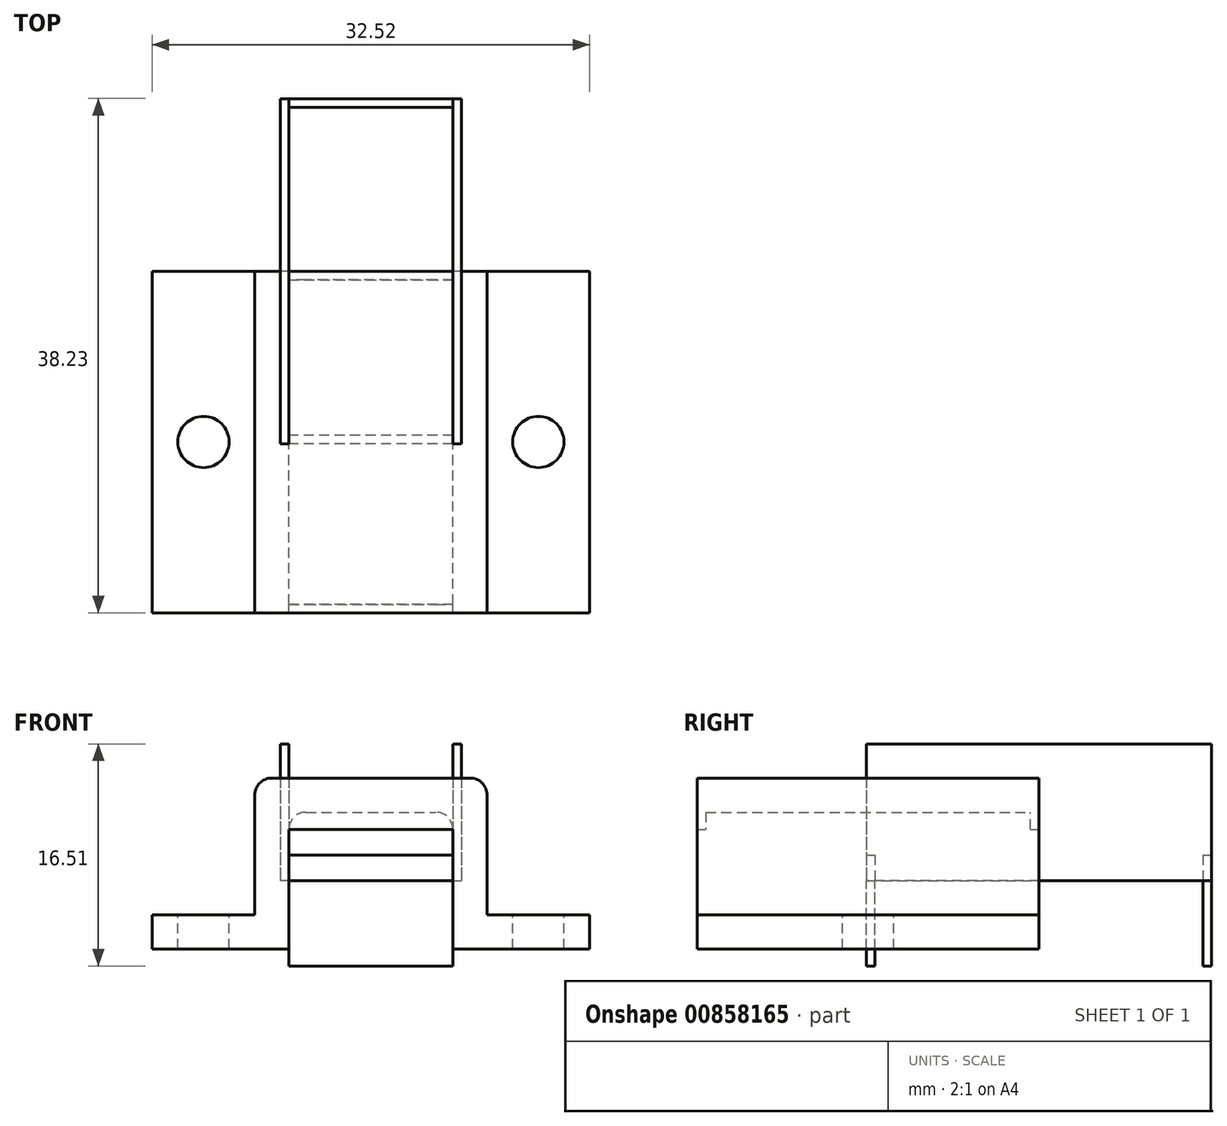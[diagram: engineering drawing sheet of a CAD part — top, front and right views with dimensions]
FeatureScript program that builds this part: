
annotation { "Feature Type Name" : "Feature", "Feature Type Description" : "" }
export const myFeature = defineFeature(function(context is Context, id is Id, definition is map)
    precondition{}
    {
        {
            var Q0;
            Q0=qCreatedBy(makeId("Top.planeOp"),FACE);
            var sketch = newSketch(context, id + "F0", { "sketchPlane" : qUnion([Q0])});
            skLineSegment(sketch, "E0.bottom", {"start": v(6.73, -12.2) * mm, "end": v(-6.73, -12.2) * mm});
            skLineSegment(sketch, "E0.top", {"start": v(6.73, 12.2) * mm, "end": v(-6.73, 12.2) * mm});
            skLineSegment(sketch, "E0.left", {"start": v(6.1, -12.83) * mm, "end": v(6.1, 12.83) * mm});
            skLineSegment(sketch, "E0.right", {"start": v(-6.1, -12.83) * mm, "end": v(-6.1, 12.83) * mm});
            skPoint(sketch, "E0.middle", {"position": v(0, 0) * mm});
            skPoint(sketch, "E1.orphan", {"position": v(-6.1, -12.2) * mm});
            skLineSegment(sketch, "E2", {"start": v(-6.1, -12.83) * mm, "end": v(-6.73, -12.83) * mm});
            skPoint(sketch, "E3.orphan", {"position": v(-6.1, 12.2) * mm});
            skPoint(sketch, "E4.orphan", {"position": v(6.1, 12.2) * mm});
            skLineSegment(sketch, "E5", {"start": v(-6.73, -12.83) * mm, "end": v(-6.73, 12.83) * mm});
            skLineSegment(sketch, "E6", {"start": v(-6.73, 12.83) * mm, "end": v(6.73, 12.83) * mm});
            skLineSegment(sketch, "E7", {"start": v(6.73, 12.83) * mm, "end": v(6.73, -12.2) * mm});
            skLineSegment(sketch, "E8", {"start": v(6.73, -12.83) * mm, "end": v(-6.1, -12.83) * mm});
            skLineSegment(sketch, "E9", {"start": v(6.73, -12.2) * mm, "end": v(6.73, -12.83) * mm});
            skPoint(sketch, "E10.orphan", {"position": v(6.1, -12.2) * mm});
            skSolve(sketch);
        }
        {
            var Q0;
            Q0=qCreatedBy(makeId("Front.planeOp"),FACE);
            var sketch = newSketch(context, id + "F1", { "sketchPlane" : qUnion([Q0])});
            skLineSegment(sketch, "E11.top", {"start": v(4.83, 5.08) * mm, "end": v(-4.83, 5.08) * mm});
            skLineSegment(sketch, "E11.left", {"start": v(6.1, -5.08) * mm, "end": v(6.1, 3.81) * mm});
            skLineSegment(sketch, "E11.right", {"start": v(-6.1, -5.08) * mm, "end": v(-6.1, 3.81) * mm});
            skPoint(sketch, "E11.middle", {"position": v(0, 0) * mm});
            skLineSegment(sketch, "E12", {"start": v(8.64, -2.54) * mm, "end": v(8.64, 6.35) * mm});
            skLineSegment(sketch, "E13", {"start": v(7.37, 7.62) * mm, "end": v(-7.37, 7.62) * mm});
            skLineSegment(sketch, "E14", {"start": v(-8.64, 6.35) * mm, "end": v(-8.64, -2.54) * mm});
            skLineSegment(sketch, "E15", {"start": v(-6.1, -5.08) * mm, "end": v(-16.26, -5.08) * mm});
            skLineSegment(sketch, "E16", {"start": v(-16.26, -5.08) * mm, "end": v(-16.26, -2.54) * mm});
            skLineSegment(sketch, "E17", {"start": v(-16.26, -2.54) * mm, "end": v(-8.64, -2.54) * mm});
            skLineSegment(sketch, "E18.MirrorCS", {"start": v(16.26, -2.54) * mm, "end": v(8.64, -2.54) * mm});
            skLineSegment(sketch, "E19.MirrorCS", {"start": v(6.1, -5.08) * mm, "end": v(16.26, -5.08) * mm});
            skLineSegment(sketch, "E20.MirrorCS", {"start": v(16.26, -5.08) * mm, "end": v(16.26, -2.54) * mm});
            skPoint(sketch, "E21.visualSharp", {"position": v(-6.1, 5.08) * mm});
            skArc(sketch, "E21.filletArc", {"start": v(-4.83, 5.08) * mm, "mid": v(-5.72, 4.7) * mm, "end": v(-6.1, 3.81) * mm});
            skPoint(sketch, "E22.visualSharp", {"position": v(6.1, 5.08) * mm});
            skArc(sketch, "E22.filletArc", {"start": v(6.1, 3.81) * mm, "mid": v(5.72, 4.7) * mm, "end": v(4.83, 5.08) * mm});
            skPoint(sketch, "E23.visualSharp", {"position": v(-8.64, 7.62) * mm});
            skArc(sketch, "E23.filletArc", {"start": v(-7.37, 7.62) * mm, "mid": v(-8.26, 7.25) * mm, "end": v(-8.64, 6.35) * mm});
            skPoint(sketch, "E24.visualSharp", {"position": v(8.64, 7.62) * mm});
            skArc(sketch, "E24.filletArc", {"start": v(8.64, 6.35) * mm, "mid": v(8.26, 7.25) * mm, "end": v(7.37, 7.62) * mm});
            skSolve(sketch);
        }
        {
            var Q0;
            Q0=makeQuery(id+"F1.imprint","IMPRINT",FACE,{"disambiguationData":[TD([[makeQuery(id+"F1.imprint","IMPRINT",EDGE,{"derivedFrom":sQuery(id+"F1.wireOp",EDGE,"E11.top")}),-1.0]])]});
            extrude(context, id + "F2", {"entities" : qUnion([Q0]), "depth" : 25.4 * mm, "offsetDistance" : 25.4 * mm});
        }
        {
            var Q0;
            Q0=makeQuery(id+"F2.opExtrude","SWEPT_FACE",FACE,{"disambiguationData":[OSD([sQuery(id+"F1.wireOp",EDGE,"E13")])]});
            var sketch = newSketch(context, id + "F3", { "sketchPlane" : qUnion([Q0])});
            skPoint(sketch, "E25", {"position": v(7.37, 0) * mm});
            skLineSegment(sketch, "E26.bottom", {"start": v(-7.38, 0) * mm, "end": v(7.37, 0) * mm});
            skLineSegment(sketch, "E26.top", {"start": v(-7.38, -0.63) * mm, "end": v(7.37, -0.63) * mm});
            skLineSegment(sketch, "E26.left", {"start": v(-7.38, 0) * mm, "end": v(-7.38, -0.63) * mm});
            skLineSegment(sketch, "E26.right", {"start": v(7.37, 0) * mm, "end": v(7.37, -0.63) * mm});
            skPoint(sketch, "E27", {"position": v(7.37, -25.4) * mm});
            skLineSegment(sketch, "E28.bottom", {"start": v(7.37, -25.4) * mm, "end": v(7.37, -25.4) * mm});
            skLineSegment(sketch, "E29.bottom", {"start": v(7.37, -25.4) * mm, "end": v(-7.37, -25.4) * mm});
            skLineSegment(sketch, "E29.top", {"start": v(7.37, -24.77) * mm, "end": v(-7.37, -24.77) * mm});
            skLineSegment(sketch, "E29.left", {"start": v(7.37, -25.4) * mm, "end": v(7.37, -24.77) * mm});
            skLineSegment(sketch, "E29.right", {"start": v(-7.37, -25.4) * mm, "end": v(-7.37, -24.77) * mm});
            skSolve(sketch);
        }
        {
            var Q0;
            {var subQ0=sQuery(id+"F3.wireOp",EDGE,"E26.right");Q0=makeQuery(id+"F3.imprint","IMPRINT",FACE,{"disambiguationData":[TD([[makeQuery(id+"F3.imprint","IMPRINT",EDGE,{"derivedFrom":subQ0}),1.0]])]});}
            var Q1;
            Q1=makeQuery(id+"F3.imprint","IMPRINT",FACE,{"disambiguationData":[TD([[makeQuery(id+"F3.imprint","IMPRINT",EDGE,{"derivedFrom":sQuery(id+"F3.wireOp",EDGE,"E28.bottom")}),-1.0]])]});
            extrude(context, id + "F4", {"entities" : qUnion([Q0, Q1]), "operationType" : NewBodyOperationType.ADD, "oppositeDirection" : true, "depth" : 3.8 * mm, "offsetDistance" : 25.4 * mm});
        }
        {
            var Q0;
            Q0=makeQuery(id+"F2.opExtrude","SWEPT_FACE",FACE,{"disambiguationData":[OSD([sQuery(id+"F1.wireOp",EDGE,"E17")])]});
            var sketch = newSketch(context, id + "F5", { "sketchPlane" : qUnion([Q0])});
            skLineSegment(sketch, "E30", {"start": v(-12.45, 0) * mm, "end": v(-12.45, -10.8) * mm});
            skPoint(sketch, "E31", {"position": v(-12.45, -12.7) * mm});
            skLineSegment(sketch, "E32.MirrorCS", {"start": v(12.45, 0) * mm, "end": v(12.45, -10.8) * mm});
            skPoint(sketch, "E33.MirrorP", {"position": v(12.45, -12.7) * mm});
            skCircle(sketch, "E34", {"center": v(-12.45, -12.7) * mm, "radius": 1.9 * mm});
            skCircle(sketch, "E35.MirrorC", {"center": v(12.45, -12.7) * mm, "radius": 1.9 * mm});
            skLineSegment(sketch, "E36.trimOffspring", {"start": v(-12.45, -14.6) * mm, "end": v(-12.45, -25.4) * mm});
            skLineSegment(sketch, "E37.trimOffspring", {"start": v(12.45, -14.6) * mm, "end": v(12.45, -25.4) * mm});
            skSolve(sketch);
        }
        {
            var Q0;
            Q0=makeQuery(id+"F3.imprint","IMPRINT",FACE,{"disambiguationData":[TD([[makeQuery(id+"F3.imprint","IMPRINT",EDGE,{"derivedFrom":sQuery(id+"F3.wireOp",EDGE,"E29.bottom")}),-1.0]])]});
            extrude(context, id + "F6", {"entities" : qUnion([Q0]), "operationType" : NewBodyOperationType.ADD, "oppositeDirection" : true, "depth" : 3.8 * mm, "offsetDistance" : 25.4 * mm});
        }
        {
            var Q0;
            Q0=sQuery(id+"F5.wireOp",VERTEX,"E31");
            var Q1;
            Q1=sQuery(id+"F5.wireOp",VERTEX,"E33.MirrorP");
            var Q2;
            Q2=makeQuery(id+"F2.opExtrude","SWEPT_BODY",BODY,{"disambiguationData":[OSD([sQuery(id+"F1.wireOp",EDGE,"E11.top"),sQuery(id+"F1.wireOp",EDGE,"E11.left"),sQuery(id+"F1.wireOp",EDGE,"E11.right"),sQuery(id+"F1.wireOp",EDGE,"E12"),sQuery(id+"F1.wireOp",EDGE,"E13"),sQuery(id+"F1.wireOp",EDGE,"E14"),sQuery(id+"F1.wireOp",EDGE,"E15"),sQuery(id+"F1.wireOp",EDGE,"E16"),sQuery(id+"F1.wireOp",EDGE,"E17"),sQuery(id+"F1.wireOp",EDGE,"E18.MirrorCS"),sQuery(id+"F1.wireOp",EDGE,"E19.MirrorCS"),sQuery(id+"F1.wireOp",EDGE,"E20.MirrorCS"),sQuery(id+"F1.wireOp",EDGE,"E21.filletArc"),sQuery(id+"F1.wireOp",EDGE,"E22.filletArc"),sQuery(id+"F1.wireOp",EDGE,"E23.filletArc"),sQuery(id+"F1.wireOp",EDGE,"E24.filletArc")])]});
            hole(context, id + "F7", {"style" : HoleStyle.SIMPLE, "endStyle" : HoleEndStyle.THROUGH, "holeDiameter" : 3.8 * mm, "majorDiameter" : 6.35 * mm, "isTappedThrough" : true, "tappedDepth" : 12.7 * mm, "tapClearance" : 3, "locations" : qUnion([Q0, Q1]), "scope" : qUnion([Q2])});
        }
        {
            var Q0;
            {var subQ5=sQuery(id+"F0.wireOp",EDGE,"E2");Q0=makeQuery(id+"F0.imprint","IMPRINT",FACE,{"disambiguationData":[TD([[makeQuery(id+"F0.imprint","IMPRINT",EDGE,{"derivedFrom":subQ5}),-1.0]])]});}
            var Q1;
            {var subQ0=sQuery(id+"F0.wireOp",EDGE,"E9");Q1=makeQuery(id+"F0.imprint","IMPRINT",FACE,{"disambiguationData":[TD([[makeQuery(id+"F0.imprint","IMPRINT",EDGE,{"derivedFrom":subQ0}),-1.0]])]});}
            var Q2;
            {var subQ0=sQuery(id+"F0.wireOp",EDGE,"E7");var subQ5=sQuery(id+"F0.wireOp",EDGE,"E0.top");var subQ6=makeQuery(id+"F0.imprint","INTERSECT",VERTEX,{"derivedFrom":[subQ5,subQ0]});Q2=makeQuery(id+"F0.imprint","IMPRINT",FACE,{"disambiguationData":[TD([[makeQuery(id+"F0.imprint","IMPRINT",EDGE,{"disambiguationData":[TD([[subQ6,-1.0]])],"derivedFrom":subQ5}),1.0]])]});}
            var Q3;
            {var subQ0=sQuery(id+"F0.wireOp",EDGE,"E7");var subQ1=sQuery(id+"F0.wireOp",EDGE,"E0.top");var subQ2=makeQuery(id+"F0.imprint","INTERSECT",VERTEX,{"derivedFrom":[subQ1,subQ0]});Q3=makeQuery(id+"F0.imprint","IMPRINT",FACE,{"disambiguationData":[TD([[makeQuery(id+"F0.imprint","IMPRINT",EDGE,{"disambiguationData":[TD([[subQ2,-1.0]])],"derivedFrom":subQ1}),-1.0]])]});}
            var Q4;
            {var subQ0=sQuery(id+"F0.wireOp",EDGE,"E5");var subQ1=sQuery(id+"F0.wireOp",EDGE,"E0.top");var subQ2=makeQuery(id+"F0.imprint","INTERSECT",VERTEX,{"derivedFrom":[subQ1,subQ0]});Q4=makeQuery(id+"F0.imprint","IMPRINT",FACE,{"disambiguationData":[TD([[makeQuery(id+"F0.imprint","IMPRINT",EDGE,{"disambiguationData":[TD([[subQ2,1.0]])],"derivedFrom":subQ1}),-1.0]])]});}
            var Q5;
            {var subQ0=sQuery(id+"F0.wireOp",EDGE,"E5");var subQ1=sQuery(id+"F0.wireOp",EDGE,"E0.bottom");var subQ2=makeQuery(id+"F0.imprint","INTERSECT",VERTEX,{"derivedFrom":[subQ1,subQ0]});Q5=makeQuery(id+"F0.imprint","IMPRINT",FACE,{"disambiguationData":[TD([[makeQuery(id+"F0.imprint","IMPRINT",EDGE,{"disambiguationData":[TD([[subQ2,1.0]])],"derivedFrom":subQ1}),-1.0]])]});}
            extrude(context, id + "F8", {"entities" : qUnion([Q0, Q1, Q2, Q3, Q4, Q5]), "depth" : 10.16 * mm, "offsetDistance" : 25.4 * mm});
        }
        {
            var Q0;
            {var subQ0=sQuery(id+"F0.wireOp",EDGE,"E0.left");var subQ1=sQuery(id+"F0.wireOp",EDGE,"E0.top");var subQ2=makeQuery(id+"F0.imprint","INTERSECT",VERTEX,{"derivedFrom":[subQ1,subQ0]});Q0=makeQuery(id+"F0.imprint","IMPRINT",FACE,{"disambiguationData":[TD([[makeQuery(id+"F0.imprint","IMPRINT",EDGE,{"disambiguationData":[TD([[subQ2,-1.0]])],"derivedFrom":subQ1}),-1.0]])]});}
            var Q1;
            {var subQ0=sQuery(id+"F0.wireOp",EDGE,"E0.left");var subQ1=sQuery(id+"F0.wireOp",EDGE,"E0.bottom");var subQ2=makeQuery(id+"F0.imprint","INTERSECT",VERTEX,{"derivedFrom":[subQ1,subQ0]});Q1=makeQuery(id+"F0.imprint","IMPRINT",FACE,{"disambiguationData":[TD([[makeQuery(id+"F0.imprint","IMPRINT",EDGE,{"disambiguationData":[TD([[subQ2,-1.0]])],"derivedFrom":subQ1}),1.0]])]});}
            extrude(context, id + "F9", {"entities" : qUnion([Q0, Q1]), "depth" : 1.9 * mm, "offsetDistance" : 25.4 * mm});
        }
        {
            var Q0;
            Q0=makeQuery(id+"F9.opExtrude","CAP_FACE",FACE,{"disambiguationData":[OSD([sQuery(id+"F0.wireOp",EDGE,"E0.top"),sQuery(id+"F0.wireOp",EDGE,"E0.left"),sQuery(id+"F0.wireOp",EDGE,"E0.right"),sQuery(id+"F0.wireOp",EDGE,"E6")])],"isStart":true});
            var Q1;
            Q1=makeQuery(id+"F9.opExtrude","CAP_FACE",FACE,{"disambiguationData":[OSD([sQuery(id+"F0.wireOp",EDGE,"E0.bottom"),sQuery(id+"F0.wireOp",EDGE,"E0.left"),sQuery(id+"F0.wireOp",EDGE,"E0.right"),sQuery(id+"F0.wireOp",EDGE,"E8")])],"isStart":true});
            extrude(context, id + "F10", {"entities" : qUnion([Q0, Q1]), "depth" : 6.35 * mm, "offsetDistance" : 25.4 * mm});
        }
    });
